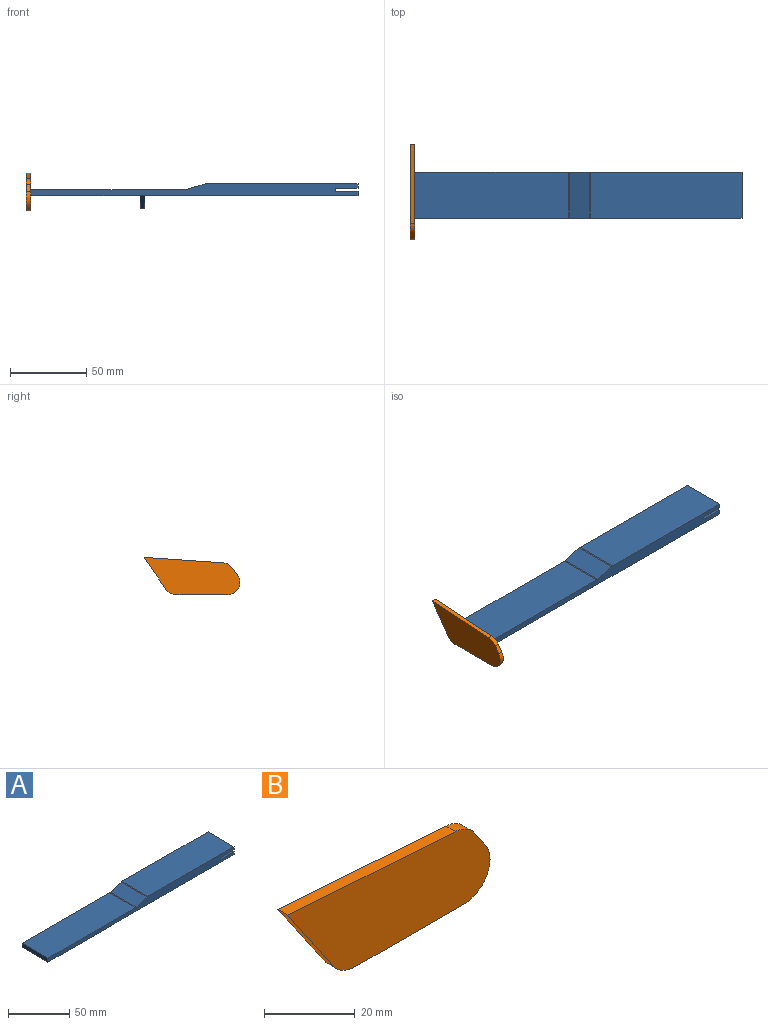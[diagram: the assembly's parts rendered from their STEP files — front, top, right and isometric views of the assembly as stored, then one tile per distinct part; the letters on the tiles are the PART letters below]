
ASSEMBLY  parts=2 mates=1
PART A: 25 faces, bbox 215x30x16 mm
  f0: plane 30x8mm, normal (-1,0,0), area 132mm2, adj f1,f3,f18,f19,f20,f21,f22,f23
  f1: plane 10x3mm, normal (0,0,-1), area 30mm2, adj f0,f2,f23,f24
  f2: plane 30x8mm, normal (1,0,0), area 132mm2, adj f1,f4,f18,f19,f20,f21,f22,f23
  f3: plane 72x30mm, normal (0,0,-1), area 2160mm2, adj f0,f6,f9,f14
  f4: plane 140x30mm, normal (0,0,-1), area 4200mm2, adj f2,f6,f10,f14
  f5: plane 30x3mm, normal (1,0,0), area 90mm2, adj f6,f11,f14,f15
  f6: plane 215x7.96mm, normal (0,-1,0), area 1253.5mm2, adj f3,f4,f5,f7,f8,f9,f10,f11
  f7: cylinder r=3mm len=30mm, axis (0,1,0), area 25.5mm2, adj f6,f8,f13,f14
  f8: plane 101x30mm, normal (0,0,1), area 3030.1mm2, adj f6,f7,f9,f14
  f9: plane 30x4mm, normal (-1,0,0), area 120mm2, adj f3,f6,f8,f14
  f10: plane 30x3mm, normal (1,0,0), area 89.4mm2, adj f4,f6,f14,f16
  f11: plane 99.57x30mm, normal (0,0,1), area 2987mm2, adj f5,f6,f12,f14
  f12: cylinder r=3mm len=30mm, axis (0,1,0), area 25.5mm2, adj f6,f11,f13,f14
  f13: plane 30x12.75mm, normal (-0.28,0,0.96), area 398.5mm2, adj f6,f7,f12,f14
  f14: plane 215x7.96mm, normal (0,1,0), area 1252.9mm2, adj f3,f4,f5,f7,f8,f9,f10,f11
  f15: plane 30x15mm, normal (0,0,-1), area 450mm2, adj f5,f6,f14,f17
  f16: plane 30x15mm, normal (0,0,1), area 450mm2, adj f6,f10,f14,f17
  f17: plane 30x2mm, normal (1,0,0), area 59.4mm2, adj f6,f14,f15,f16
  f18: cylinder r=4.76mm len=9.41mm, axis (-1,0,0), area 40.5mm2, adj f0,f2,f19,f21
  f19: plane 3x2mm, normal (0,0,1), area 6mm2, adj f0,f2,f18,f20
  f20: cylinder r=2.8mm len=5.41mm, axis (-1,0,0), area 22mm2, adj f0,f2,f19,f21
  f21: plane 3x2mm, normal (0,0,1), area 6mm2, adj f0,f2,f18,f20
  f22: cylinder r=1.55mm len=3.1mm, axis (-1,0,0), area 29.2mm2, adj f0,f2
  f23: plane 10x8mm, normal (0,-0.62,-0.78), area 38.4mm2, adj f0,f1,f2,f6
  f24: plane 10x8mm, normal (0,0.62,-0.78), area 38.4mm2, adj f0,f1,f2,f14
PART B: 9 faces, bbox 62.9x3x24.5 mm
  f0: plane 34x3mm, normal (0,0,-1), area 102mm2, adj f1,f6,f7,f8
  f1: cylinder r=8mm len=12.51mm, axis (0,1,0), area 52.1mm2, adj f0,f2,f7,f8
  f2: plane 4.85x3.31mm, normal (0.83,0,0.56), area 17.6mm2, adj f1,f3,f7,f8
  f3: cylinder r=8mm len=6.05mm, axis (0,1,0), area 21.7mm2, adj f2,f4,f7,f8
  f4: plane 52.17x3.62mm, normal (0.07,0,1), area 156.9mm2, adj f3,f5,f7,f8
  f5: plane 20.97x14.32mm, normal (-0.83,0,-0.56), area 76.2mm2, adj f4,f6,f7,f8
  f6: cylinder r=8mm len=6.61mm, axis (0,1,0), area 23.3mm2, adj f0,f5,f7,f8
  f7: plane 62.93x24.45mm, normal (0,-1,0), area 1144.8mm2, adj f0,f1,f2,f3,f4,f5,f6
  f8: plane 62.93x24.45mm, normal (0,1,0), area 1144.8mm2, adj f0,f1,f2,f3,f4,f5,f6
PLACE A t=(31.18,-16.25,8.41)mm
PLACE B rot(axis=(0,0,-1),90deg) t=(-158.82,-33.69,13.32)mm
MATE fastened B.f8 <-> A.f9  axis (1,0,0) through (-158.82,-31.25,10.41)mm
